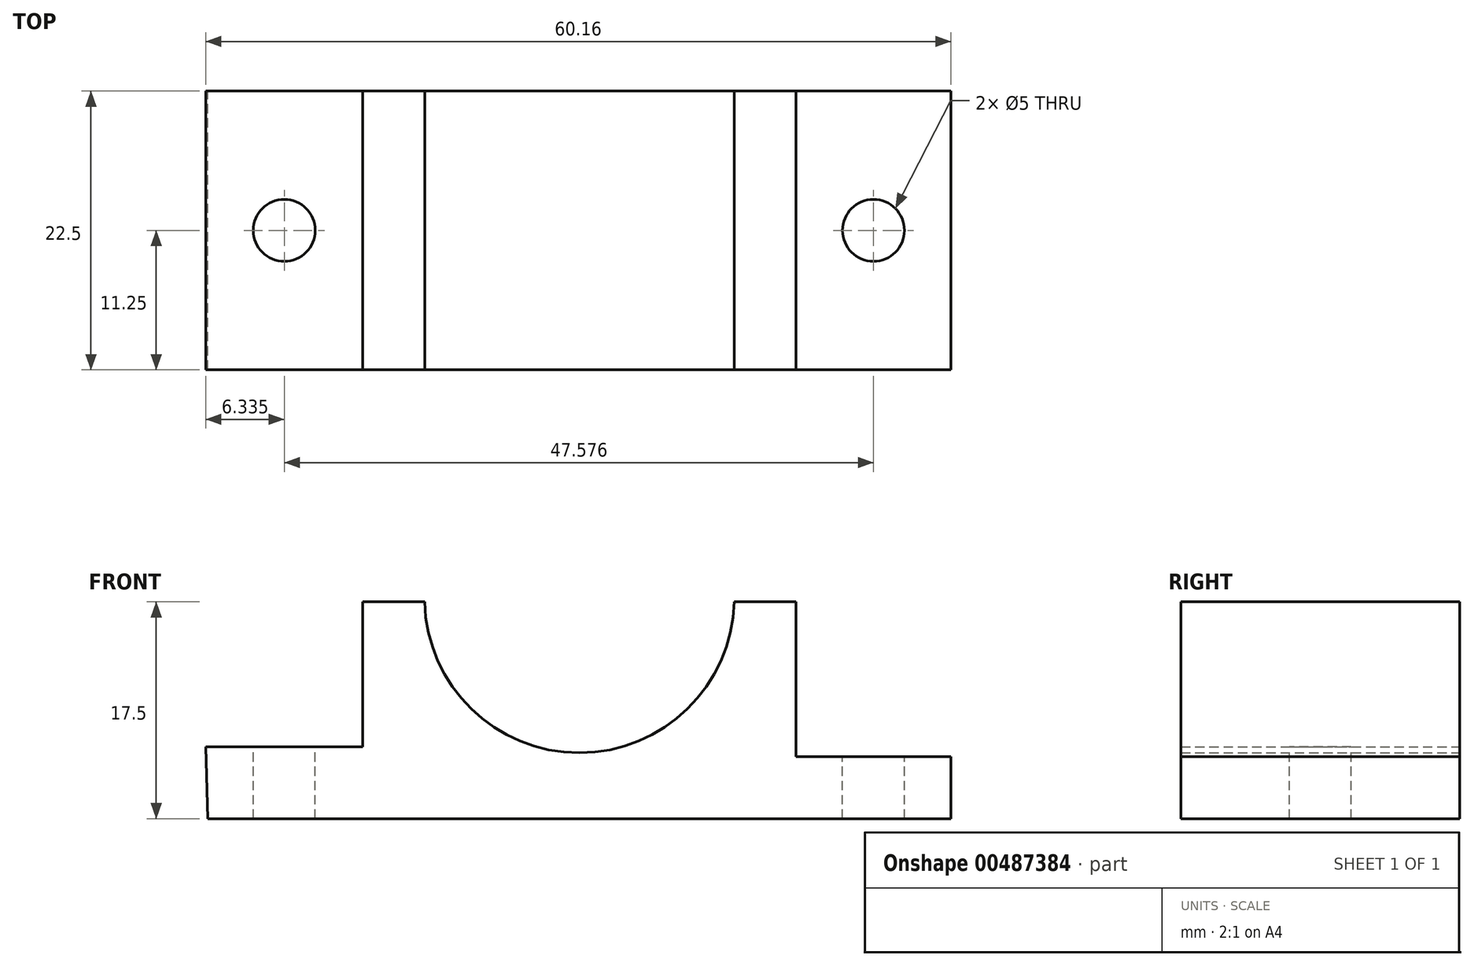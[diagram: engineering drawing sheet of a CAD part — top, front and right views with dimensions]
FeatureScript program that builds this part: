
annotation { "Feature Type Name" : "Feature", "Feature Type Description" : "" }
export const myFeature = defineFeature(function(context is Context, id is Id, definition is map)
    precondition{}
    {
        {
            var Q0;
            Q0=qCreatedBy(makeId("Front.planeOp"),FACE);
            var sketch = newSketch(context, id + "F0", { "sketchPlane" : qUnion([Q0])});
            skLineSegment(sketch, "E0", {"start": v(-27.05, 0) * mm, "end": v(32.95, 0) * mm});
            skLineSegment(sketch, "E1", {"start": v(32.95, 0) * mm, "end": v(32.95, 5) * mm});
            skLineSegment(sketch, "E2", {"start": v(32.95, 5) * mm, "end": v(20.45, 5) * mm});
            skLineSegment(sketch, "E3", {"start": v(20.45, 5) * mm, "end": v(20.45, 17.5) * mm});
            skLineSegment(sketch, "E4", {"start": v(-14.54, 17.5) * mm, "end": v(-14.54, 5.8) * mm});
            skLineSegment(sketch, "E5", {"start": v(-14.54, 5.8) * mm, "end": v(-14.7, 5.8) * mm});
            skLineSegment(sketch, "E6", {"start": v(-14.7, 5.8) * mm, "end": v(-27.2, 5.8) * mm});
            skLineSegment(sketch, "E7", {"start": v(-27.2, 5.8) * mm, "end": v(-27.05, 0) * mm});
            skLineSegment(sketch, "E8", {"start": v(-14.54, 17.5) * mm, "end": v(-9.54, 17.5) * mm});
            skLineSegment(sketch, "E9", {"start": v(15.45, 17.5) * mm, "end": v(20.45, 17.5) * mm});
            skArc(sketch, "E10", {"start": v(-9.54, 17.5) * mm, "mid": v(2.96, 5.3) * mm, "end": v(15.45, 17.5) * mm});
            skSolve(sketch);
        }
        {
            var Q0;
            Q0=makeQuery(id+"F0.imprint","IMPRINT",FACE,{"disambiguationData":[TD([[makeQuery(id+"F0.imprint","IMPRINT",EDGE,{"derivedFrom":sQuery(id+"F0.wireOp",EDGE,"E0")}),1.0]])]});
            extrude(context, id + "F1", {"entities" : qUnion([Q0]), "depth" : 22.5 * mm});
        }
        {
            var Q0;
            Q0=makeQuery(id+"F1.opExtrude","SWEPT_FACE",FACE,{"disambiguationData":[OSD([sQuery(id+"F0.wireOp",EDGE,"E2")])]});
            var sketch = newSketch(context, id + "F2", { "sketchPlane" : qUnion([Q0])});
            skCircle(sketch, "E11", {"center": v(26.7, -11.25) * mm, "radius": 2.5 * mm});
            skSolve(sketch);
        }
        {
            var Q0;
            Q0=makeQuery(id+"F2.imprint","IMPRINT",FACE,{"disambiguationData":[TD([[makeQuery(id+"F2.imprint","IMPRINT",EDGE,{"derivedFrom":sQuery(id+"F2.wireOp",EDGE,"E11")}),1.0]])]});
            extrude(context, id + "F3", {"entities" : qUnion([Q0]), "operationType" : NewBodyOperationType.REMOVE, "endBound" : BoundingType.THROUGH_ALL, "oppositeDirection" : true, "depth" : 25 * mm});
        }
        {
            var Q0;
            Q0=makeQuery(id+"F1.opExtrude","SWEPT_FACE",FACE,{"disambiguationData":[OSD([sQuery(id+"F0.wireOp",EDGE,"E5"),sQuery(id+"F0.wireOp",EDGE,"E6")])]});
            var sketch = newSketch(context, id + "F4", { "sketchPlane" : qUnion([Q0])});
            skCircle(sketch, "E12", {"center": v(-20.87, -11.25) * mm, "radius": 2.5 * mm});
            skSolve(sketch);
        }
        {
            var Q0;
            Q0=makeQuery(id+"F4.imprint","IMPRINT",FACE,{"disambiguationData":[TD([[makeQuery(id+"F4.imprint","IMPRINT",EDGE,{"derivedFrom":sQuery(id+"F4.wireOp",EDGE,"E12")}),1.0]])]});
            extrude(context, id + "F5", {"entities" : qUnion([Q0]), "operationType" : NewBodyOperationType.REMOVE, "endBound" : BoundingType.THROUGH_ALL, "oppositeDirection" : true, "depth" : 25 * mm});
        }
    });
